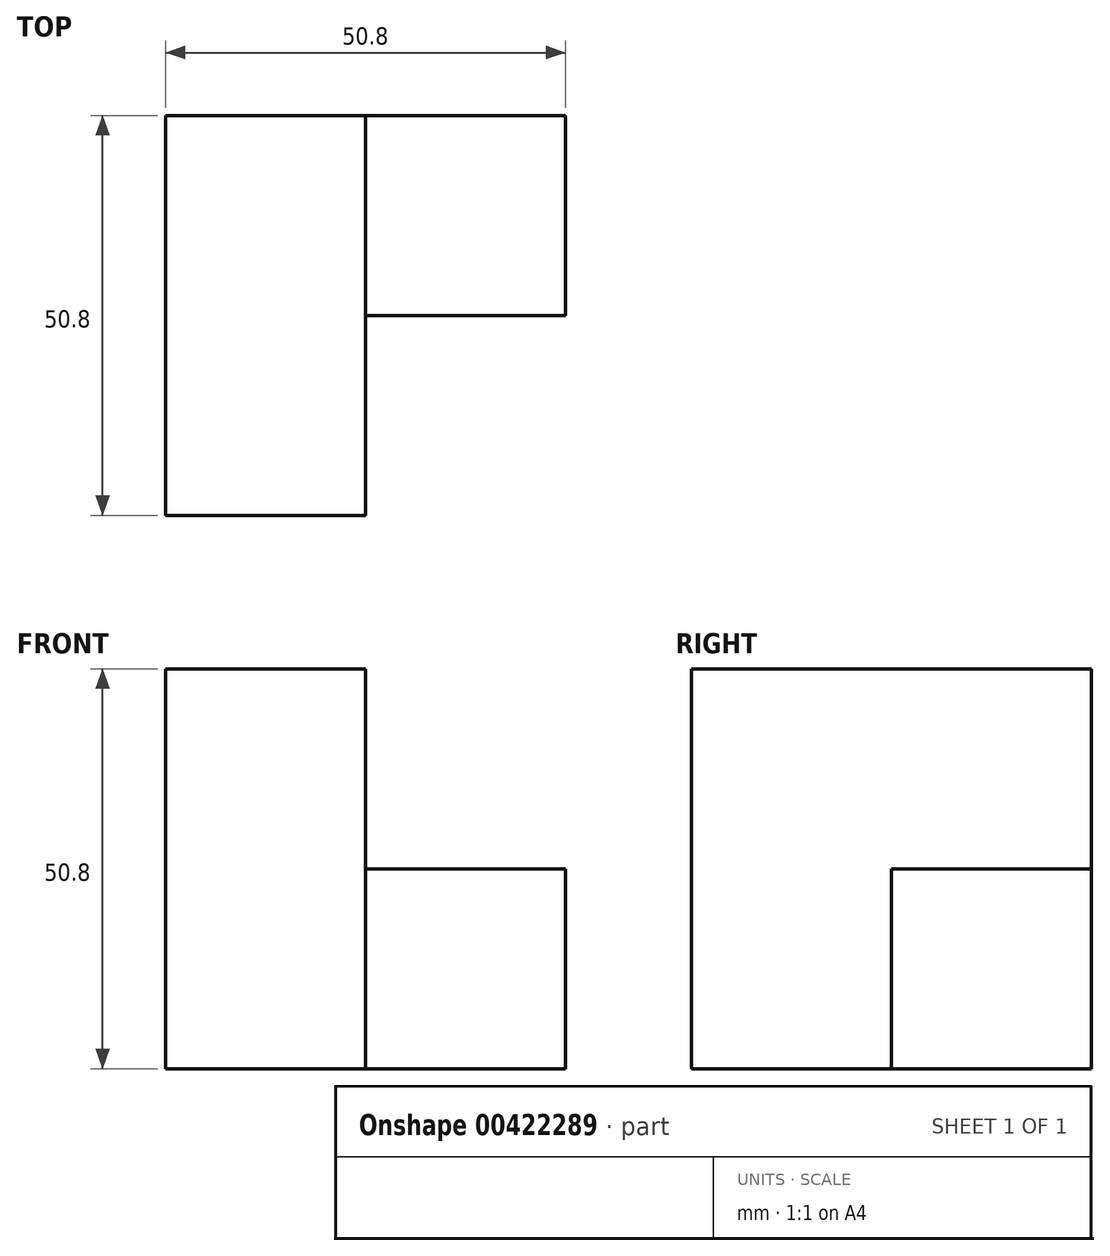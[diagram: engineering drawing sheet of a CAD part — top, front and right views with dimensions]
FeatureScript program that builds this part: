
annotation { "Feature Type Name" : "Feature", "Feature Type Description" : "" }
export const myFeature = defineFeature(function(context is Context, id is Id, definition is map)
    precondition{}
    {
        {
            var Q0;
            Q0=qCreatedBy(makeId("Front.planeOp"),FACE);
            var sketch = newSketch(context, id + "F0", { "sketchPlane" : qUnion([Q0])});
            skLineSegment(sketch, "E0.bottom", {"start": v(0, 0) * mm, "end": v(-25.4, 0) * mm});
            skLineSegment(sketch, "E0.top", {"start": v(0, 50.8) * mm, "end": v(-25.4, 50.8) * mm});
            skLineSegment(sketch, "E0.left", {"start": v(0, 0) * mm, "end": v(0, 50.8) * mm});
            skLineSegment(sketch, "E0.right", {"start": v(-25.4, 0) * mm, "end": v(-25.4, 50.8) * mm});
            skSolve(sketch);
        }
        {
            var Q0;
            Q0=qCreatedBy(makeId("Front.planeOp"),FACE);
            var sketch = newSketch(context, id + "F1", { "sketchPlane" : qUnion([Q0])});
            skLineSegment(sketch, "E1.bottom", {"start": v(0, 0) * mm, "end": v(25.4, 0) * mm});
            skLineSegment(sketch, "E1.top", {"start": v(0, 25.4) * mm, "end": v(25.4, 25.4) * mm});
            skLineSegment(sketch, "E1.left", {"start": v(0, 0) * mm, "end": v(0, 25.4) * mm});
            skLineSegment(sketch, "E1.right", {"start": v(25.4, 0) * mm, "end": v(25.4, 25.4) * mm});
            skSolve(sketch);
        }
        {
            var Q0;
            Q0 = qSketchRegion(id + "F1", true);
            extrude(context, id + "F2", {"entities" : qUnion([Q0]), "depth" : 25.4 * mm});
        }
        {
            var Q0;
            Q0 = qSketchRegion(id + "F0", true);
            extrude(context, id + "F3", {"entities" : qUnion([Q0]), "operationType" : NewBodyOperationType.ADD, "depth" : 50.8 * mm});
        }
    });
